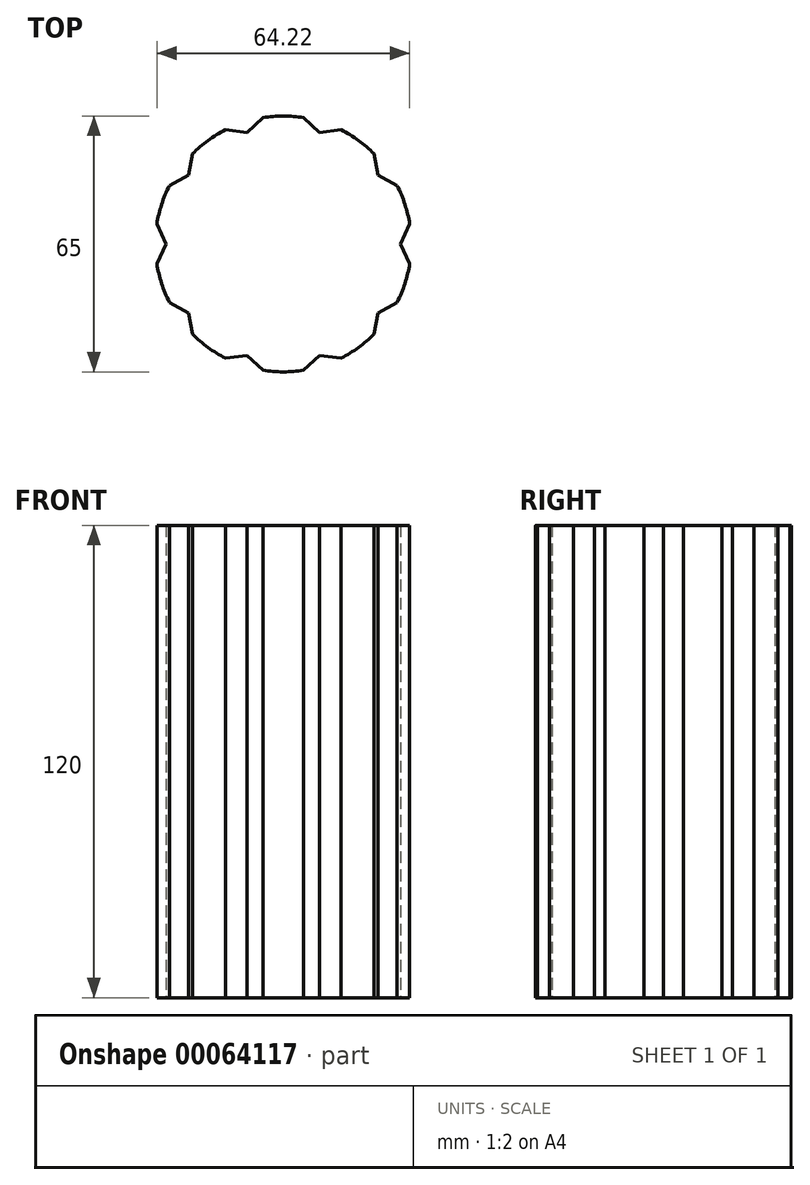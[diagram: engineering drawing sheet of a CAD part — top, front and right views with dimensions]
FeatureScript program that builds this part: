
annotation { "Feature Type Name" : "Feature", "Feature Type Description" : "" }
export const myFeature = defineFeature(function(context is Context, id is Id, definition is map)
    precondition{}
    {
        {
            var Q0;
            Q0=qCreatedBy(makeId("Top.planeOp"),FACE);
            var sketch = newSketch(context, id + "F0", { "sketchPlane" : qUnion([Q0])});
            skCircle(sketch, "E0", {"center": v(0, 0) * mm, "radius": 32.5 * mm, "construction": true});
            skArc(sketch, "E1", {"start": v(5.18, 32.09) * mm, "mid": v(0, 32.5) * mm, "end": v(-5.17, 32.09) * mm});
            skLineSegment(sketch, "E2", {"start": v(-5.17, 32.09) * mm, "end": v(-9.2, 28.32) * mm});
            skLineSegment(sketch, "E3", {"start": v(-9.2, 28.32) * mm, "end": v(-14.68, 29) * mm});
            skLineSegment(sketch, "E4", {"start": v(5.18, 32.09) * mm, "end": v(9.2, 28.32) * mm});
            skLineSegment(sketch, "E5", {"start": v(9.2, 28.32) * mm, "end": v(14.68, 29) * mm});
            skLineSegment(sketch, "E6.1.0", {"start": v(-23.05, 22.92) * mm, "end": v(-24.1, 17.5) * mm});
            skArc(sketch, "E6.1.1", {"start": v(-14.67, 29) * mm, "mid": v(-19.1, 26.3) * mm, "end": v(-23.05, 22.92) * mm});
            skLineSegment(sketch, "E6.1.2", {"start": v(-14.67, 29) * mm, "end": v(-9.2, 28.33) * mm});
            skLineSegment(sketch, "E6.2.0", {"start": v(-32.11, 5) * mm, "end": v(-29.78, 0) * mm});
            skArc(sketch, "E6.2.1", {"start": v(-28.92, 14.84) * mm, "mid": v(-30.9, 10.04) * mm, "end": v(-32.11, 5) * mm});
            skLineSegment(sketch, "E6.2.2", {"start": v(-28.92, 14.84) * mm, "end": v(-24.1, 17.51) * mm});
            skLineSegment(sketch, "E6.3.0", {"start": v(-28.92, -14.84) * mm, "end": v(-24.1, -17.51) * mm});
            skArc(sketch, "E6.3.1", {"start": v(-32.11, -5) * mm, "mid": v(-30.9, -10.04) * mm, "end": v(-28.92, -14.84) * mm});
            skLineSegment(sketch, "E6.3.2", {"start": v(-32.11, -5) * mm, "end": v(-29.78, 0) * mm});
            skLineSegment(sketch, "E6.4.0", {"start": v(-14.67, -29) * mm, "end": v(-9.2, -28.33) * mm});
            skArc(sketch, "E6.4.1", {"start": v(-23.05, -22.92) * mm, "mid": v(-19.1, -26.3) * mm, "end": v(-14.67, -29) * mm});
            skLineSegment(sketch, "E6.4.2", {"start": v(-23.05, -22.92) * mm, "end": v(-24.1, -17.5) * mm});
            skLineSegment(sketch, "E6.5.0", {"start": v(5.17, -32.09) * mm, "end": v(9.2, -28.32) * mm});
            skArc(sketch, "E6.5.1", {"start": v(-5.18, -32.09) * mm, "mid": v(0, -32.5) * mm, "end": v(5.17, -32.09) * mm});
            skLineSegment(sketch, "E6.5.2", {"start": v(-5.18, -32.09) * mm, "end": v(-9.2, -28.32) * mm});
            skLineSegment(sketch, "E7.2.6.0", {"start": v(23.05, -22.92) * mm, "end": v(24.1, -17.5) * mm});
            skArc(sketch, "E7.3.6.0", {"start": v(14.67, -29) * mm, "mid": v(19.1, -26.3) * mm, "end": v(23.05, -22.92) * mm});
            skLineSegment(sketch, "E7.7.6.0", {"start": v(14.67, -29) * mm, "end": v(9.2, -28.33) * mm});
            skLineSegment(sketch, "E8.2.7.0", {"start": v(32.11, -5) * mm, "end": v(29.78, 0) * mm});
            skArc(sketch, "E8.3.7.0", {"start": v(28.92, -14.84) * mm, "mid": v(30.9, -10.04) * mm, "end": v(32.11, -5) * mm});
            skLineSegment(sketch, "E8.7.7.0", {"start": v(28.92, -14.84) * mm, "end": v(24.1, -17.51) * mm});
            skLineSegment(sketch, "E9.2.8.0", {"start": v(28.92, 14.84) * mm, "end": v(24.1, 17.51) * mm});
            skArc(sketch, "E9.3.8.0", {"start": v(32.11, 5) * mm, "mid": v(30.9, 10.04) * mm, "end": v(28.92, 14.84) * mm});
            skLineSegment(sketch, "E9.7.8.0", {"start": v(32.11, 5) * mm, "end": v(29.78, 0) * mm});
            skLineSegment(sketch, "E9.2.9.0", {"start": v(14.67, 29) * mm, "end": v(9.2, 28.33) * mm});
            skArc(sketch, "E9.3.9.0", {"start": v(23.05, 22.92) * mm, "mid": v(19.1, 26.3) * mm, "end": v(14.67, 29) * mm});
            skLineSegment(sketch, "E9.7.9.0", {"start": v(23.05, 22.92) * mm, "end": v(24.1, 17.5) * mm});
            skSolve(sketch);
        }
        {
            var Q0;
            {var subQ32=sQuery(id+"F0.wireOp",EDGE,"E1");Q0=makeQuery(id+"F0.imprint","IMPRINT",FACE,{"disambiguationData":[TD([[makeQuery(id+"F0.imprint","IMPRINT",EDGE,{"derivedFrom":subQ32}),1.0]])]});}
            extrude(context, id + "F1", {"entities" : qUnion([Q0]), "depth" : 120 * mm});
        }
    });
